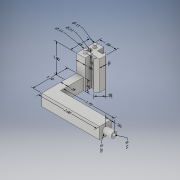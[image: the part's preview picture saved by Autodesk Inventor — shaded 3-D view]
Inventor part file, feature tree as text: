
AUTODESK INVENTOR PART (.ipt)
format: ipt  version: 2018 (Build 220112000, 112)  size: 204,800 bytes
history: native  units: in
note: dims shown in document units (in); Inventor stores cm internally (conversion verified against a paired STEP export)
features: other x19, sketch x7, extrude x5, hole x2
ambient origin geometry x8: Origin, YZ Plane, XZ Plane, XY Plane, X Axis, Y Axis, Z Axis, Center Point
bodies: Solid1 (feature_tree)
feature tree (33):
  other  "Annotations"
  extrude  "Extrusion1"  Depth=0.65in
  extrude  "Extrusion2"  Depth=0.28in
  hole  "Hole1"  [1 undecoded]
  extrude  "Extrusion6"  Depth=0.1in
  extrude  "Extrusion7"  Depth=1.0in
  extrude  "Extrusion8"  Depth=0.11in
  hole  "Hole3"  [1 undecoded]
  sketch  "Sketch1"  dims[d0=0.3in d1=0.65in]
  sketch  "Sketch2"  dims[d2=0.225in d3=0.28in]
  sketch  "Sketch3"  dims[d4=0.2in d5=0.1in]
  sketch  "Sketch8"  dims[d6=0.1in d7=0.1in]
  sketch  "Sketch9"  dims[d8=1.0in d9=0.0in d10=0.16in]
  sketch  "Sketch10"  dims[d11=0.16in d12=0.11in]
  sketch  "Sketch11"  dims[d13=0.11in d14=0.1in d15=0.0in d16=0.325in d17=0.11in d18=0.75in d19=0.375in d20=0.25in d21=0.5635in d22=0.45in d23=0.8108in d43=0.25in d44=0.4in d45=1.2in d46=0.0in d47=0.4in d48=1.75in d49=0.0in d50=0.2in d51=0.2in d52=0.3in d53=0.0in d54=0.11in d55=0.11in d56=0.75in d57=0.375in d58=0.25in d59=0.5635in d60=0.63in d61=0.8108in d100=1.75in d101=1.6183in d102=0.11in d103=0.3in d104=1.0578in d105=0.2in d62=0.2035in d63=0.1468in d64=0.65in d65=0.1815in d66=0.174in d67=0.58in d68=0.3163in d69=0.2492in d70=0.3in d71=0.1702in d72=1.0in d73=2.4081in d74=0.11in d75=2.3346in d76=0.11in d77=2.1934in d78=0.11in d79=0.1in d80=0.3393in d81=0.3689in d82=0.2in d83=0.1398in d84=0.3767in d85=0.2828in d86=0.0327in d87=0.2433in d88=1.2in d89=0.0in d90=0.3937in d91=0.4in d92=0.2788in d93=0.3314in d94=2.0in d95=0.3446in d96=0.2116in d97=0.25in d98=0.1292in d99=0.3512in]
  other  "Linear Dimension 1"
  other  "Linear Dimension 2"
  other  "Linear Dimension 3"
  other  "Linear Dimension 4"
  other  "Diameter Dimension 1"
  other  "Diameter Dimension 2"
  other  "Diameter Dimension 3"
  other  "Linear Dimension 5"
  other  "Linear Dimension 6"
  other  "Linear Dimension 7"
  other  "Linear Dimension 8"
  other  "Linear Dimension 9"
  other  "Linear Dimension 10"
  other  "Linear Dimension 11"
  other  "Linear Dimension 12"
  other  "Diameter Dimension 4"
  other  "Linear Dimension 13"
  other  "Diameter Dimension 5"
note: 2 required parameter values undecoded (feature->parameter linkage not recoverable at this tier; creation-order binding heuristic only, values carry confidence <= 0.55)
